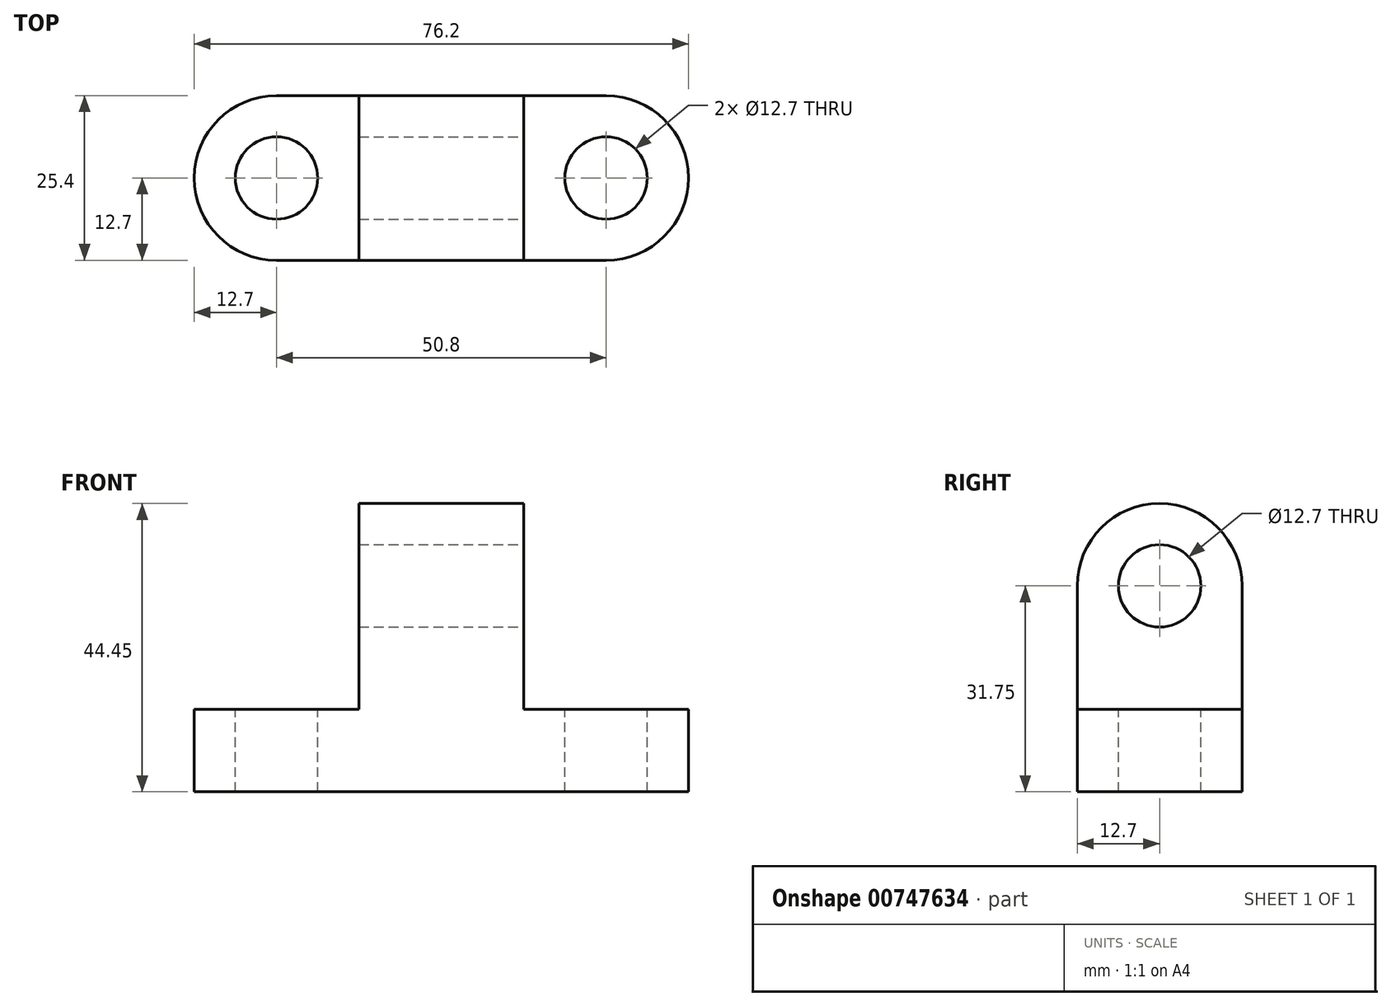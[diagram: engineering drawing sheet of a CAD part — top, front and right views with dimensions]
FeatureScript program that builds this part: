
annotation { "Feature Type Name" : "Feature", "Feature Type Description" : "" }
export const myFeature = defineFeature(function(context is Context, id is Id, definition is map)
    precondition{}
    {
        {
            var Q0;
            Q0=qCreatedBy(makeId("Front.planeOp"),FACE);
            var sketch = newSketch(context, id + "F0", { "sketchPlane" : qUnion([Q0])});
            skLineSegment(sketch, "E0", {"start": v(0, 0) * mm, "end": v(76.2, 0) * mm});
            skLineSegment(sketch, "E1", {"start": v(76.2, 0) * mm, "end": v(76.2, 44.45) * mm});
            skLineSegment(sketch, "E2", {"start": v(76.2, 44.45) * mm, "end": v(0, 44.45) * mm});
            skLineSegment(sketch, "E3", {"start": v(0, 44.45) * mm, "end": v(0, 0) * mm});
            skSolve(sketch);
        }
        {
            var Q0;
            Q0=makeQuery(id+"F0.imprint","IMPRINT",FACE,{"disambiguationData":[TD([[makeQuery(id+"F0.imprint","IMPRINT",EDGE,{"derivedFrom":sQuery(id+"F0.wireOp",EDGE,"E0")}),1.0]])]});
            extrude(context, id + "F1", {"entities" : qUnion([Q0]), "oppositeDirection" : true, "depth" : 25.4 * mm, "offsetDistance" : 25.4 * mm});
        }
        {
            var Q0;
            Q0=makeQuery(id+"F1.opExtrude","CAP_FACE",FACE,{"disambiguationData":[OSD([sQuery(id+"F0.wireOp",EDGE,"E0"),sQuery(id+"F0.wireOp",EDGE,"E1"),sQuery(id+"F0.wireOp",EDGE,"E2"),sQuery(id+"F0.wireOp",EDGE,"E3")])],"isStart":true});
            var sketch = newSketch(context, id + "F2", { "sketchPlane" : qUnion([Q0])});
            skLineSegment(sketch, "E4", {"start": v(25.4, 44.45) * mm, "end": v(25.4, 12.7) * mm});
            skLineSegment(sketch, "E5", {"start": v(25.4, 12.7) * mm, "end": v(0, 12.7) * mm});
            skLineSegment(sketch, "E6", {"start": v(50.8, 44.45) * mm, "end": v(50.8, 12.7) * mm});
            skLineSegment(sketch, "E7", {"start": v(50.8, 12.7) * mm, "end": v(76.2, 12.7) * mm});
            skSolve(sketch);
        }
        {
            var Q0;
            Q0 = qSketchRegion(id + "F2", true);
            var Q1;
            {var subQ0=sQuery(id+"F2.wireOp",EDGE,"E4");Q1=makeQuery(id+"F2.imprint","IMPRINT",FACE,{"disambiguationData":[TD([[makeQuery(id+"F2.imprint","IMPRINT",EDGE,{"derivedFrom":subQ0}),-1.0]])]});}
            var Q2;
            {var subQ0=sQuery(id+"F2.wireOp",EDGE,"E6");Q2=makeQuery(id+"F2.imprint","IMPRINT",FACE,{"disambiguationData":[TD([[makeQuery(id+"F2.imprint","IMPRINT",EDGE,{"derivedFrom":subQ0}),1.0]])]});}
            extrude(context, id + "F3", {"entities" : qUnion([Q0, Q1, Q2]), "operationType" : NewBodyOperationType.REMOVE, "oppositeDirection" : true, "depth" : 25.4 * mm, "offsetDistance" : 25.4 * mm});
        }
        {
            var Q0;
            Q0=makeQuery(id+"F3.boolean.opBoolean","COPY",FACE,{"derivedFrom":makeQuery(id+"F3.opExtrude","SWEPT_FACE",FACE,{"disambiguationData":[OSD([sQuery(id+"F2.wireOp",EDGE,"E6")])]})});
            var sketch = newSketch(context, id + "F4", { "sketchPlane" : qUnion([Q0])});
            skCircle(sketch, "E8", {"center": v(12.7, 31.75) * mm, "radius": 6.35 * mm});
            skArc(sketch, "E9", {"start": v(25.4, 31.75) * mm, "mid": v(12.7, 44.45) * mm, "end": v(0, 31.75) * mm});
            skSolve(sketch);
        }
        {
            var Q0;
            Q0=makeQuery(id+"F4.imprint","IMPRINT",FACE,{"disambiguationData":[TD([[makeQuery(id+"F4.imprint","IMPRINT",EDGE,{"derivedFrom":sQuery(id+"F4.wireOp",EDGE,"E8")}),1.0]])]});
            var Q1;
            {var subQ0=sQuery(id+"F4.wireOp",EDGE,"E9");var subQ1=sQuery(id+"F2.wireOp",EDGE,"E6");var subQ2=makeQuery(id+"F3.boolean.opBoolean","COPY",EDGE,{"derivedFrom":makeQuery(id+"F3.opExtrude","CAP_EDGE",EDGE,{"disambiguationData":[OSD([subQ1])],"isStart":false})});var subQ3=makeQuery(id+"F4.imprint","INTERSECT",VERTEX,{"derivedFrom":[subQ2,subQ0]});Q1=makeQuery(id+"F4.imprint","IMPRINT",FACE,{"disambiguationData":[TD([[makeQuery(id+"F4.imprint","IMPRINT",EDGE,{"disambiguationData":[TD([[subQ3,-1.0]])],"derivedFrom":subQ0}),-1.0]])]});}
            var Q2;
            {var subQ0=sQuery(id+"F4.wireOp",EDGE,"E9");var subQ1=sQuery(id+"F2.wireOp",EDGE,"E6");var subQ2=makeQuery(id+"F3.boolean.opBoolean","COPY",EDGE,{"derivedFrom":makeQuery(id+"F3.opExtrude","CAP_EDGE",EDGE,{"disambiguationData":[OSD([subQ1])],"isStart":true})});var subQ3=makeQuery(id+"F4.imprint","INTERSECT",VERTEX,{"derivedFrom":[subQ2,subQ0]});Q2=makeQuery(id+"F4.imprint","IMPRINT",FACE,{"disambiguationData":[TD([[makeQuery(id+"F4.imprint","IMPRINT",EDGE,{"disambiguationData":[TD([[subQ3,1.0]])],"derivedFrom":subQ0}),-1.0]])]});}
            extrude(context, id + "F5", {"entities" : qUnion([Q0, Q1, Q2]), "operationType" : NewBodyOperationType.REMOVE, "oppositeDirection" : true, "depth" : 25.4 * mm, "offsetDistance" : 25.4 * mm});
        }
        {
            var Q0;
            Q0=makeQuery(id+"F3.boolean.opBoolean","COPY",FACE,{"derivedFrom":makeQuery(id+"F3.opExtrude","SWEPT_FACE",FACE,{"disambiguationData":[OSD([sQuery(id+"F2.wireOp",EDGE,"E5")])]})});
            var sketch = newSketch(context, id + "F6", { "sketchPlane" : qUnion([Q0])});
            skCircle(sketch, "E10", {"center": v(12.7, 12.7) * mm, "radius": 6.35 * mm});
            skCircle(sketch, "E11", {"center": v(61.83, 13.18) * mm, "radius": 7.15 * mm});
            skArc(sketch, "E12", {"start": v(12.7, 25.4) * mm, "mid": v(0, 12.7) * mm, "end": v(12.7, 0) * mm});
            skSolve(sketch);
        }
        {
            var Q0;
            Q0=makeQuery(id+"F6.imprint","IMPRINT",FACE,{"disambiguationData":[TD([[makeQuery(id+"F6.imprint","IMPRINT",EDGE,{"derivedFrom":sQuery(id+"F6.wireOp",EDGE,"E10")}),1.0]])]});
            var Q1;
            {var subQ0=sQuery(id+"F6.wireOp",EDGE,"E12");var subQ1=sQuery(id+"F2.wireOp",EDGE,"E5");var subQ2=makeQuery(id+"F3.boolean.opBoolean","COPY",EDGE,{"derivedFrom":makeQuery(id+"F3.opExtrude","CAP_EDGE",EDGE,{"disambiguationData":[OSD([subQ1])],"isStart":false})});var subQ3=makeQuery(id+"F6.imprint","INTERSECT",VERTEX,{"derivedFrom":[subQ2,subQ0]});Q1=makeQuery(id+"F6.imprint","IMPRINT",FACE,{"disambiguationData":[TD([[makeQuery(id+"F6.imprint","IMPRINT",EDGE,{"disambiguationData":[TD([[subQ3,-1.0]])],"derivedFrom":subQ0}),-1.0]])]});}
            var Q2;
            {var subQ0=sQuery(id+"F6.wireOp",EDGE,"E12");var subQ1=sQuery(id+"F2.wireOp",EDGE,"E5");var subQ2=makeQuery(id+"F3.boolean.opBoolean","COPY",EDGE,{"derivedFrom":makeQuery(id+"F3.opExtrude","CAP_EDGE",EDGE,{"disambiguationData":[OSD([subQ1])],"isStart":true})});var subQ3=makeQuery(id+"F6.imprint","INTERSECT",VERTEX,{"derivedFrom":[subQ2,subQ0]});Q2=makeQuery(id+"F6.imprint","IMPRINT",FACE,{"disambiguationData":[TD([[makeQuery(id+"F6.imprint","IMPRINT",EDGE,{"disambiguationData":[TD([[subQ3,1.0]])],"derivedFrom":subQ0}),-1.0]])]});}
            extrude(context, id + "F7", {"entities" : qUnion([Q0, Q1, Q2]), "operationType" : NewBodyOperationType.REMOVE, "oppositeDirection" : true, "depth" : 25.4 * mm, "offsetDistance" : 25.4 * mm});
        }
        {
            var Q0;
            Q0=makeQuery(id+"F3.boolean.opBoolean","COPY",FACE,{"derivedFrom":makeQuery(id+"F3.opExtrude","SWEPT_FACE",FACE,{"disambiguationData":[OSD([sQuery(id+"F2.wireOp",EDGE,"E7")])]})});
            var sketch = newSketch(context, id + "F8", { "sketchPlane" : qUnion([Q0])});
            skCircle(sketch, "E13", {"center": v(63.5, 12.7) * mm, "radius": 6.35 * mm});
            skArc(sketch, "E14", {"start": v(63.5, 0) * mm, "mid": v(76.2, 12.7) * mm, "end": v(63.5, 25.4) * mm});
            skSolve(sketch);
        }
        {
            var Q0;
            Q0 = qSketchRegion(id + "F8", true);
            var Q1;
            {var subQ0=sQuery(id+"F8.wireOp",EDGE,"E14");var subQ1=sQuery(id+"F2.wireOp",EDGE,"E7");var subQ2=makeQuery(id+"F3.boolean.opBoolean","COPY",EDGE,{"derivedFrom":makeQuery(id+"F3.opExtrude","CAP_EDGE",EDGE,{"disambiguationData":[OSD([subQ1])],"isStart":true})});var subQ3=makeQuery(id+"F8.imprint","INTERSECT",VERTEX,{"derivedFrom":[subQ2,subQ0]});Q1=makeQuery(id+"F8.imprint","IMPRINT",FACE,{"disambiguationData":[TD([[makeQuery(id+"F8.imprint","IMPRINT",EDGE,{"disambiguationData":[TD([[subQ3,-1.0]])],"derivedFrom":subQ0}),-1.0]])]});}
            var Q2;
            {var subQ0=sQuery(id+"F8.wireOp",EDGE,"E14");var subQ1=sQuery(id+"F2.wireOp",EDGE,"E7");var subQ2=makeQuery(id+"F3.boolean.opBoolean","COPY",EDGE,{"derivedFrom":makeQuery(id+"F3.opExtrude","CAP_EDGE",EDGE,{"disambiguationData":[OSD([subQ1])],"isStart":false})});var subQ3=makeQuery(id+"F8.imprint","INTERSECT",VERTEX,{"derivedFrom":[subQ2,subQ0]});Q2=makeQuery(id+"F8.imprint","IMPRINT",FACE,{"disambiguationData":[TD([[makeQuery(id+"F8.imprint","IMPRINT",EDGE,{"disambiguationData":[TD([[subQ3,1.0]])],"derivedFrom":subQ0}),-1.0]])]});}
            extrude(context, id + "F9", {"entities" : qUnion([Q0, Q1, Q2]), "operationType" : NewBodyOperationType.REMOVE, "oppositeDirection" : true, "depth" : 25.4 * mm, "offsetDistance" : 25.4 * mm});
        }
    });
